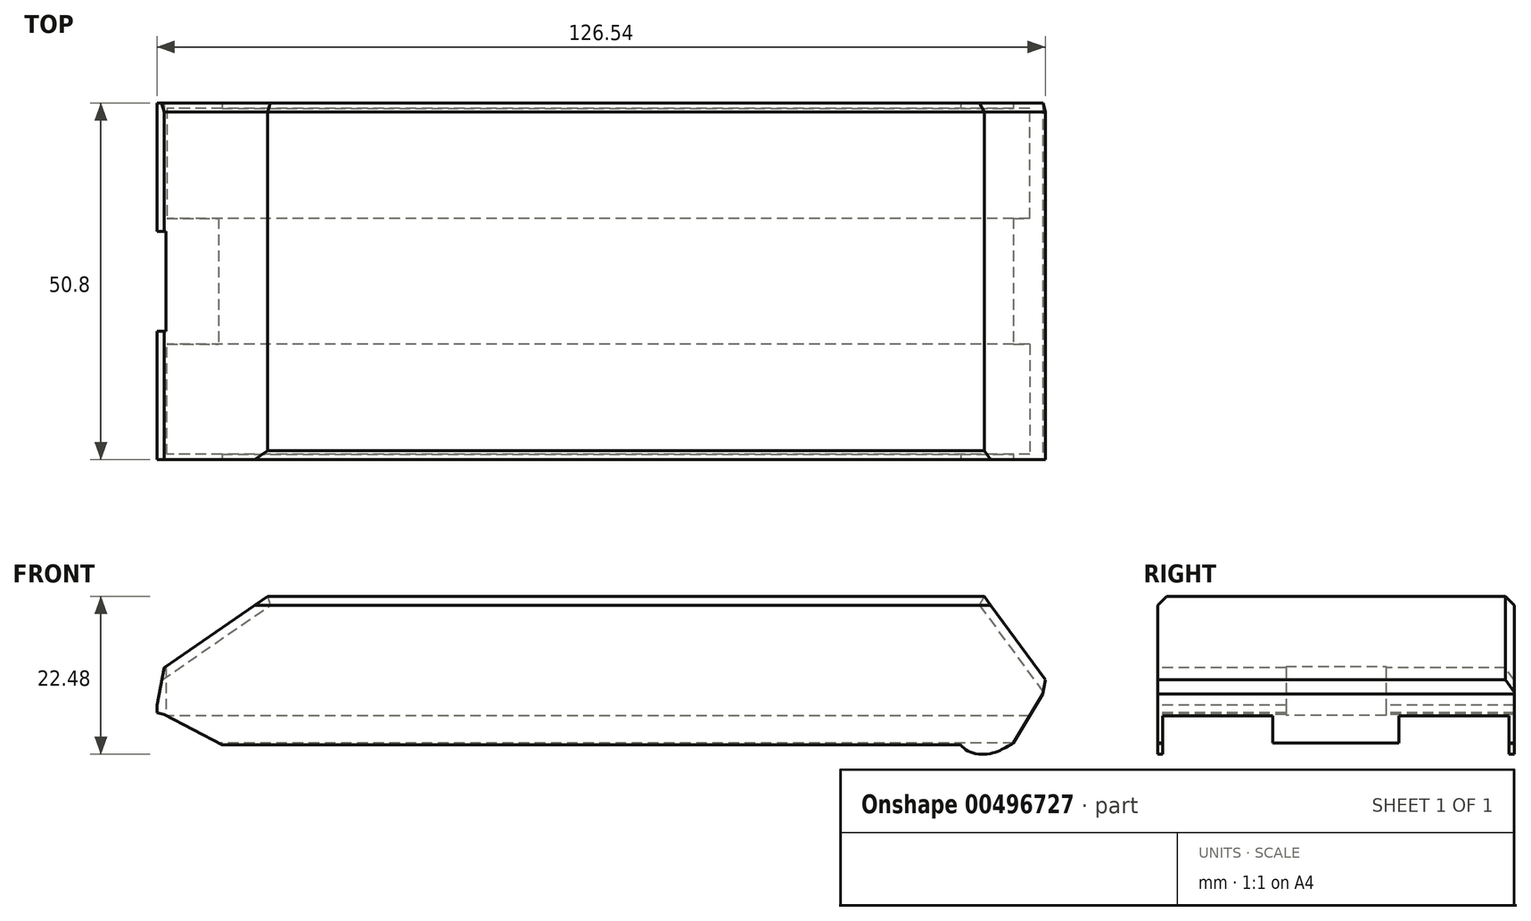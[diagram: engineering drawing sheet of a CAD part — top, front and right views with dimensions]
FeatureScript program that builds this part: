
annotation { "Feature Type Name" : "Feature", "Feature Type Description" : "" }
export const myFeature = defineFeature(function(context is Context, id is Id, definition is map)
    precondition{}
    {
        {
            var Q0;
            Q0=qCreatedBy(makeId("Top.planeOp"),FACE);
            var sketch = newSketch(context, id + "F0", { "sketchPlane" : qUnion([Q0])});
            skLineSegment(sketch, "E0", {"start": v(67.98, -23.5) * mm, "end": v(67.98, -74.3) * mm});
            skLineSegment(sketch, "E1", {"start": v(67.98, -74.3) * mm, "end": v(67.98, -48.9) * mm});
            skLineSegment(sketch, "E2", {"start": v(67.98, -48.9) * mm, "end": v(-83.66, -48.9) * mm, "construction": true});
            skLineSegment(sketch, "E3", {"start": v(67.98, -74.3) * mm, "end": v(-59.02, -74.3) * mm});
            skLineSegment(sketch, "E4", {"start": v(-59.02, -74.3) * mm, "end": v(-59.02, -56) * mm});
            skLineSegment(sketch, "E5", {"start": v(-59.02, -56) * mm, "end": v(-57.75, -56) * mm});
            skLineSegment(sketch, "E6", {"start": v(-57.75, -56) * mm, "end": v(-57.75, -48.9) * mm});
            skLineSegment(sketch, "E7.MirrorCS", {"start": v(-57.75, -41.78) * mm, "end": v(-57.75, -48.9) * mm});
            skLineSegment(sketch, "E8.MirrorCS", {"start": v(-59.02, -41.78) * mm, "end": v(-57.75, -41.78) * mm});
            skLineSegment(sketch, "E9.MirrorCS", {"start": v(-59.02, -23.5) * mm, "end": v(-59.02, -41.78) * mm});
            skLineSegment(sketch, "E10.MirrorCS", {"start": v(67.98, -23.5) * mm, "end": v(-59.02, -23.5) * mm});
            skLineSegment(sketch, "E11.MirrorCS", {"start": v(67.98, -23.5) * mm, "end": v(67.98, -48.9) * mm});
            skLineSegment(sketch, "E12", {"start": v(26.33, 80.05) * mm, "end": v(70.47, 80.05) * mm, "construction": true});
            skLineSegment(sketch, "E13", {"start": v(57.69, 39.67) * mm, "end": v(57.69, 80.05) * mm, "construction": true});
            skLineSegment(sketch, "E14", {"start": v(41.88, 60.81) * mm, "end": v(76.75, 60.81) * mm, "construction": true});
            skLineSegment(sketch, "E15", {"start": v(57.69, 39.67) * mm, "end": v(57.69, 60.81) * mm, "construction": true});
            skLineSegment(sketch, "E16", {"start": v(48.55, 62.27) * mm, "end": v(76.75, 62.27) * mm, "construction": true});
            skLineSegment(sketch, "E17", {"start": v(57.69, 62.27) * mm, "end": v(57.69, 39.67) * mm});
            skSolve(sketch);
        }
        {
            var Q0;
            Q0=qSketchRegion(id+"F0",true);
            extrude(context, id + "F1", {"entities" : qUnion([Q0]), "depth" : 22.6 * mm});
        }
        {
            var Q0;
            Q0=makeQuery(id+"F1.opExtrude","SWEPT_FACE",FACE,{"disambiguationData":[OSD([sQuery(id+"F0.wireOp",EDGE,"E3")])]});
            var sketch = newSketch(context, id + "F2", { "sketchPlane" : qUnion([Q0])});
            skLineSegment(sketch, "E18", {"start": v(-49.77, 1.46) * mm, "end": v(-57.98, 5.78) * mm});
            skLineSegment(sketch, "E19", {"start": v(-49.77, 1.46) * mm, "end": v(55.46, 1.46) * mm});
            skLineSegment(sketch, "E20", {"start": v(-59.22, 6.08) * mm, "end": v(-58.02, 12.44) * mm});
            skLineSegment(sketch, "E21", {"start": v(-57.98, 5.78) * mm, "end": v(-59.22, 6.08) * mm});
            skLineSegment(sketch, "E22", {"start": v(-58.02, 12.44) * mm, "end": v(-43.29, 22.6) * mm});
            skLineSegment(sketch, "E23", {"start": v(-43.29, 22.6) * mm, "end": v(58.82, 22.6) * mm});
            skLineSegment(sketch, "E24", {"start": v(58.82, 22.6) * mm, "end": v(67.52, 10.72) * mm});
            skLineSegment(sketch, "E25", {"start": v(67.52, 10.72) * mm, "end": v(67.18, 8.71) * mm});
            skLineSegment(sketch, "E26", {"start": v(67.18, 8.71) * mm, "end": v(63, 1.73) * mm});
            skFitSpline(sketch, "E27", {"points": [v(55.46, 1.46) * mm, v(56.6, 0.55) * mm, v(58.63, 0.13) * mm, v(60.6, 0.48) * mm, v(61.89, 1.1) * mm, v(63, 1.73) * mm], "startDerivative": vector(5.35, -5.36) * mm, "endDerivative": vector(5.72, 3.94) * mm});
            skSolve(sketch);
        }
        {
            var Q0;
            {var subQ0=sQuery(id+"F2.wireOp",EDGE,"E22");Q0=makeQuery(id+"F2.imprint","IMPRINT",FACE,{"disambiguationData":[TD([[makeQuery(id+"F2.imprint","IMPRINT",EDGE,{"derivedFrom":subQ0}),1.0]])]});}
            var Q1;
            {var subQ5=sQuery(id+"F2.wireOp",EDGE,"E18");Q1=makeQuery(id+"F2.imprint","IMPRINT",FACE,{"disambiguationData":[TD([[makeQuery(id+"F2.imprint","IMPRINT",EDGE,{"derivedFrom":subQ5}),1.0]])]});}
            extrude(context, id + "F3", {"entities" : qUnion([Q0, Q1]), "operationType" : NewBodyOperationType.REMOVE, "oppositeDirection" : true, "depth" : 56.64 * mm});
        }
        {
            var Q0;
            Q0=makeQuery(id+"F1.opExtrude","SWEPT_FACE",FACE,{"disambiguationData":[OSD([sQuery(id+"F0.wireOp",EDGE,"E6"),sQuery(id+"F0.wireOp",EDGE,"E7.MirrorCS")])]});
            var sketch = newSketch(context, id + "F4", { "sketchPlane" : qUnion([Q0])});
            skPoint(sketch, "E28.0", {"position": v(48.9, 0) * mm});
            skLineSegment(sketch, "E29", {"start": v(48.9, 0) * mm, "end": v(48.9, 46.18) * mm, "construction": true});
            skPoint(sketch, "E29.endSnap0", {"position": v(48.9, 12.63) * mm});
            skLineSegment(sketch, "E30", {"start": v(24.23, 5.57) * mm, "end": v(24.23, 0.58) * mm});
            skLineSegment(sketch, "E31", {"start": v(39.93, 0.58) * mm, "end": v(39.93, 5.57) * mm});
            skLineSegment(sketch, "E32", {"start": v(39.93, 5.57) * mm, "end": v(24.23, 5.57) * mm});
            skLineSegment(sketch, "E33.MirrorCS", {"start": v(57.86, 5.57) * mm, "end": v(73.56, 5.57) * mm});
            skLineSegment(sketch, "E34.MirrorCS", {"start": v(73.56, 5.57) * mm, "end": v(73.56, 0.58) * mm});
            skLineSegment(sketch, "E35.MirrorCS", {"start": v(57.86, 0.58) * mm, "end": v(57.86, 5.57) * mm});
            skLineSegment(sketch, "E36", {"start": v(24.23, 0.58) * mm, "end": v(24.23, -3.52) * mm});
            skLineSegment(sketch, "E37", {"start": v(24.23, -3.52) * mm, "end": v(39.93, -3.52) * mm});
            skLineSegment(sketch, "E38", {"start": v(39.93, -3.52) * mm, "end": v(39.93, 0.58) * mm});
            skLineSegment(sketch, "E39.MirrorCS", {"start": v(57.86, -3.52) * mm, "end": v(57.86, 0.58) * mm});
            skLineSegment(sketch, "E40.MirrorCS", {"start": v(73.56, -3.52) * mm, "end": v(57.86, -3.52) * mm});
            skLineSegment(sketch, "E41.MirrorCS", {"start": v(73.56, 0.58) * mm, "end": v(73.56, -3.52) * mm});
            skSolve(sketch);
        }
        {
            var Q0;
            Q0=makeQuery(id+"F4.imprint","IMPRINT",FACE,{"disambiguationData":[TD([[makeQuery(id+"F4.imprint","IMPRINT",EDGE,{"derivedFrom":sQuery(id+"F4.wireOp",EDGE,"E30")}),1.0]])]});
            var Q1;
            Q1=makeQuery(id+"F4.imprint","IMPRINT",FACE,{"disambiguationData":[TD([[makeQuery(id+"F4.imprint","IMPRINT",EDGE,{"derivedFrom":sQuery(id+"F4.wireOp",EDGE,"E33.MirrorCS")}),-1.0]])]});
            extrude(context, id + "F5", {"entities" : qUnion([Q0, Q1]), "operationType" : NewBodyOperationType.REMOVE, "oppositeDirection" : true, "depth" : 123.95 * mm});
        }
        {
            var Q0;
            Q0=makeQuery(id+"F1.opExtrude","SWEPT_FACE",FACE,{"disambiguationData":[OSD([sQuery(id+"F0.wireOp",EDGE,"E6"),sQuery(id+"F0.wireOp",EDGE,"E7.MirrorCS")])]});
            var sketch = newSketch(context, id + "F6", { "sketchPlane" : qUnion([Q0])});
            skPoint(sketch, "E42.0", {"position": v(39.93, 1.73) * mm});
            skPoint(sketch, "E43.0", {"position": v(57.86, 1.73) * mm});
            skLineSegment(sketch, "E44", {"start": v(57.86, 1.73) * mm, "end": v(39.93, 1.73) * mm});
            skLineSegment(sketch, "E45", {"start": v(39.93, -2) * mm, "end": v(57.86, -2) * mm});
            skLineSegment(sketch, "E46", {"start": v(57.86, -2) * mm, "end": v(57.86, 1.73) * mm});
            skLineSegment(sketch, "E47", {"start": v(39.93, 1.73) * mm, "end": v(39.93, -2) * mm});
            skSolve(sketch);
        }
        {
            var Q0;
            Q0=makeQuery(id+"F6.imprint","IMPRINT",FACE,{"disambiguationData":[TD([[makeQuery(id+"F6.imprint","IMPRINT",EDGE,{"derivedFrom":sQuery(id+"F6.wireOp",EDGE,"E44")}),1.0]])]});
            extrude(context, id + "F7", {"entities" : qUnion([Q0]), "operationType" : NewBodyOperationType.REMOVE, "oppositeDirection" : true, "depth" : 131.32 * mm});
        }
        {
            var Q0;
            Q0=makeQuery(id+"F3.boolean.opBoolean","INTERSECT",EDGE,{"derivedFrom":[makeQuery(id+"F1.opExtrude","SWEPT_FACE",FACE,{"disambiguationData":[OSD([sQuery(id+"F0.wireOp",EDGE,"E10.MirrorCS")])]}),makeQuery(id+"F3.opExtrude","SWEPT_FACE",FACE,{"disambiguationData":[OSD([sQuery(id+"F2.wireOp",EDGE,"E22")])]})]});
            var Q1;
            Q1=makeQuery(id+"F3.boolean.opBoolean","COPY",EDGE,{"derivedFrom":makeQuery(id+"F3.opExtrude","CAP_EDGE",EDGE,{"disambiguationData":[OSD([sQuery(id+"F2.wireOp",EDGE,"E22")])],"isStart":true})});
            var Q2;
            Q2=makeQuery(id+"F1.opExtrude","CAP_EDGE",EDGE,{"disambiguationData":[OSD([sQuery(id+"F0.wireOp",EDGE,"E10.MirrorCS")])],"isStart":false});
            var Q3;
            Q3=makeQuery(id+"F1.opExtrude","CAP_EDGE",EDGE,{"disambiguationData":[OSD([sQuery(id+"F0.wireOp",EDGE,"E3")])],"isStart":false});
            var Q4;
            Q4=makeQuery(id+"F3.boolean.opBoolean","COPY",EDGE,{"derivedFrom":makeQuery(id+"F3.opExtrude","CAP_EDGE",EDGE,{"disambiguationData":[OSD([sQuery(id+"F2.wireOp",EDGE,"E24")])],"isStart":true})});
            var Q5;
            Q5=makeQuery(id+"F3.boolean.opBoolean","INTERSECT",EDGE,{"derivedFrom":[makeQuery(id+"F1.opExtrude","SWEPT_FACE",FACE,{"disambiguationData":[OSD([sQuery(id+"F0.wireOp",EDGE,"E10.MirrorCS")])]}),makeQuery(id+"F3.opExtrude","SWEPT_FACE",FACE,{"disambiguationData":[OSD([sQuery(id+"F2.wireOp",EDGE,"E24")])]})]});
            chamfer(context, id + "F8", {"entities" : qUnion([Q0, Q1, Q2, Q3, Q4, Q5]), "width" : 1.27 * mm, "tangentPropagation" : true});
        }
    });
